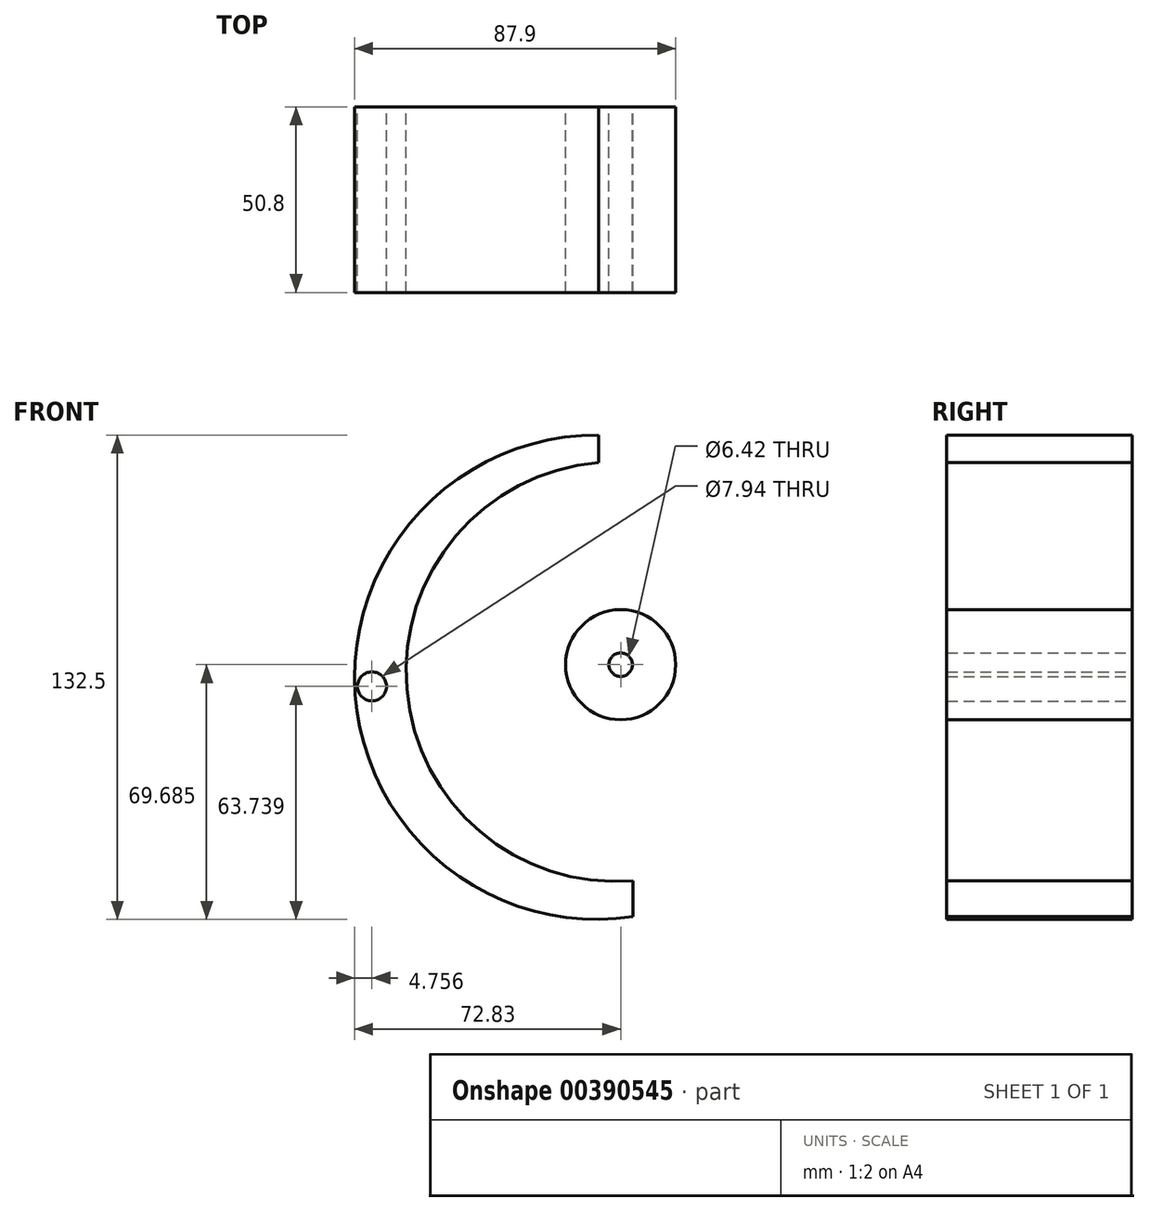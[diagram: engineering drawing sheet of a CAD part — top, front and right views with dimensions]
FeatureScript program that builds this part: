
annotation { "Feature Type Name" : "Feature", "Feature Type Description" : "" }
export const myFeature = defineFeature(function(context is Context, id is Id, definition is map)
    precondition{}
    {
        {
            var Q0;
            Q0=qCreatedBy(makeId("Front.planeOp"),FACE);
            var sketch = newSketch(context, id + "F0", { "sketchPlane" : qUnion([Q0])});
            skCircle(sketch, "E0", {"center": v(13.96, 33.5) * mm, "radius": 15.07 * mm});
            skArc(sketch, "E1", {"start": v(7.9, 88.8) * mm, "mid": v(-44.58, 26.88) * mm, "end": v(17.34, -25.6) * mm});
            skLineSegment(sketch, "E2", {"start": v(7.9, 88.8) * mm, "end": v(7.9, 96.32) * mm});
            skLineSegment(sketch, "E3", {"start": v(17.34, -25.6) * mm, "end": v(17.34, -35.42) * mm});
            skArc(sketch, "E4", {"start": v(7.9, 96.32) * mm, "mid": v(-58.7, 25.34) * mm, "end": v(17.34, -35.42) * mm});
            skCircle(sketch, "E5", {"center": v(-54.11, 27.56) * mm, "radius": 3.97 * mm});
            skCircle(sketch, "E6", {"center": v(13.96, 33.5) * mm, "radius": 3.2 * mm});
            skSolve(sketch);
        }
        {
            var Q0;
            Q0 = qSketchRegion(id + "F0", true);
            extrude(context, id + "F1", {"entities" : qUnion([Q0]), "depth" : 50.8 * mm});
        }
    });
